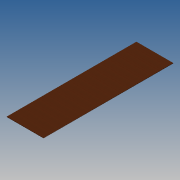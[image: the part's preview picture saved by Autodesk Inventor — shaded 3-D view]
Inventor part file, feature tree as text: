
AUTODESK INVENTOR PART (.ipt)
format: ipt  version: 2013 (Build 170138000, 138)  size: 71,680 bytes
history: native  units: in
note: dims shown in document units (in); Inventor stores cm internally (conversion verified against a paired STEP export)
features: extrude x1, sketch x1
ambient origin geometry x8: Origin, YZ Plane, XZ Plane, XY Plane, X Axis, Y Axis, Z Axis, Center Point
bodies: Solid1 (feature_tree)
feature tree (2):
  extrude  "Extrusion1"  Depth=48.0in
  sketch  "Sketch1"  dims[d0=169.0in d1=48.0in d2=0.5in d3=0.0in]
